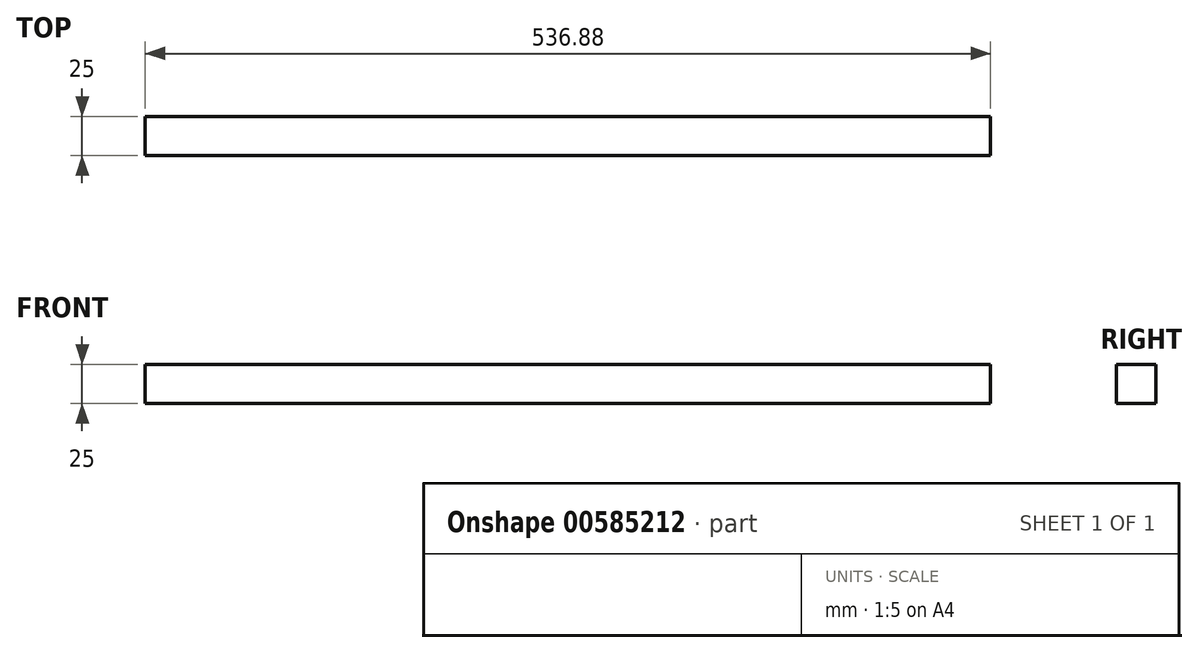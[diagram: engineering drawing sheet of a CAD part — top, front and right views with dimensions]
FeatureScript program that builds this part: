
annotation { "Feature Type Name" : "Feature", "Feature Type Description" : "" }
export const myFeature = defineFeature(function(context is Context, id is Id, definition is map)
    precondition{}
    {
        {
            var Q0;
            Q0=qCreatedBy(makeId("Front.planeOp"),FACE);
            var sketch = newSketch(context, id + "F0", { "sketchPlane" : qUnion([Q0])});
            skLineSegment(sketch, "E0.bottom", {"start": v(0, 0) * mm, "end": v(536.88, 0) * mm});
            skLineSegment(sketch, "E0.top", {"start": v(0, 25) * mm, "end": v(536.88, 25) * mm});
            skLineSegment(sketch, "E0.left", {"start": v(0, 0) * mm, "end": v(0, 25) * mm});
            skLineSegment(sketch, "E0.right", {"start": v(536.88, 0) * mm, "end": v(536.88, 25) * mm});
            skSolve(sketch);
        }
        {
            var Q0;
            Q0=makeQuery(id+"F0.imprint","IMPRINT",FACE,{"disambiguationData":[TD([[makeQuery(id+"F0.imprint","IMPRINT",EDGE,{"derivedFrom":sQuery(id+"F0.wireOp",EDGE,"E0.bottom")}),1.0]])]});
            extrude(context, id + "F1", {"entities" : qUnion([Q0]), "endBound" : BoundingType.SYMMETRIC, "depth" : 25 * mm, "offsetDistance" : 25 * mm});
        }
    });
